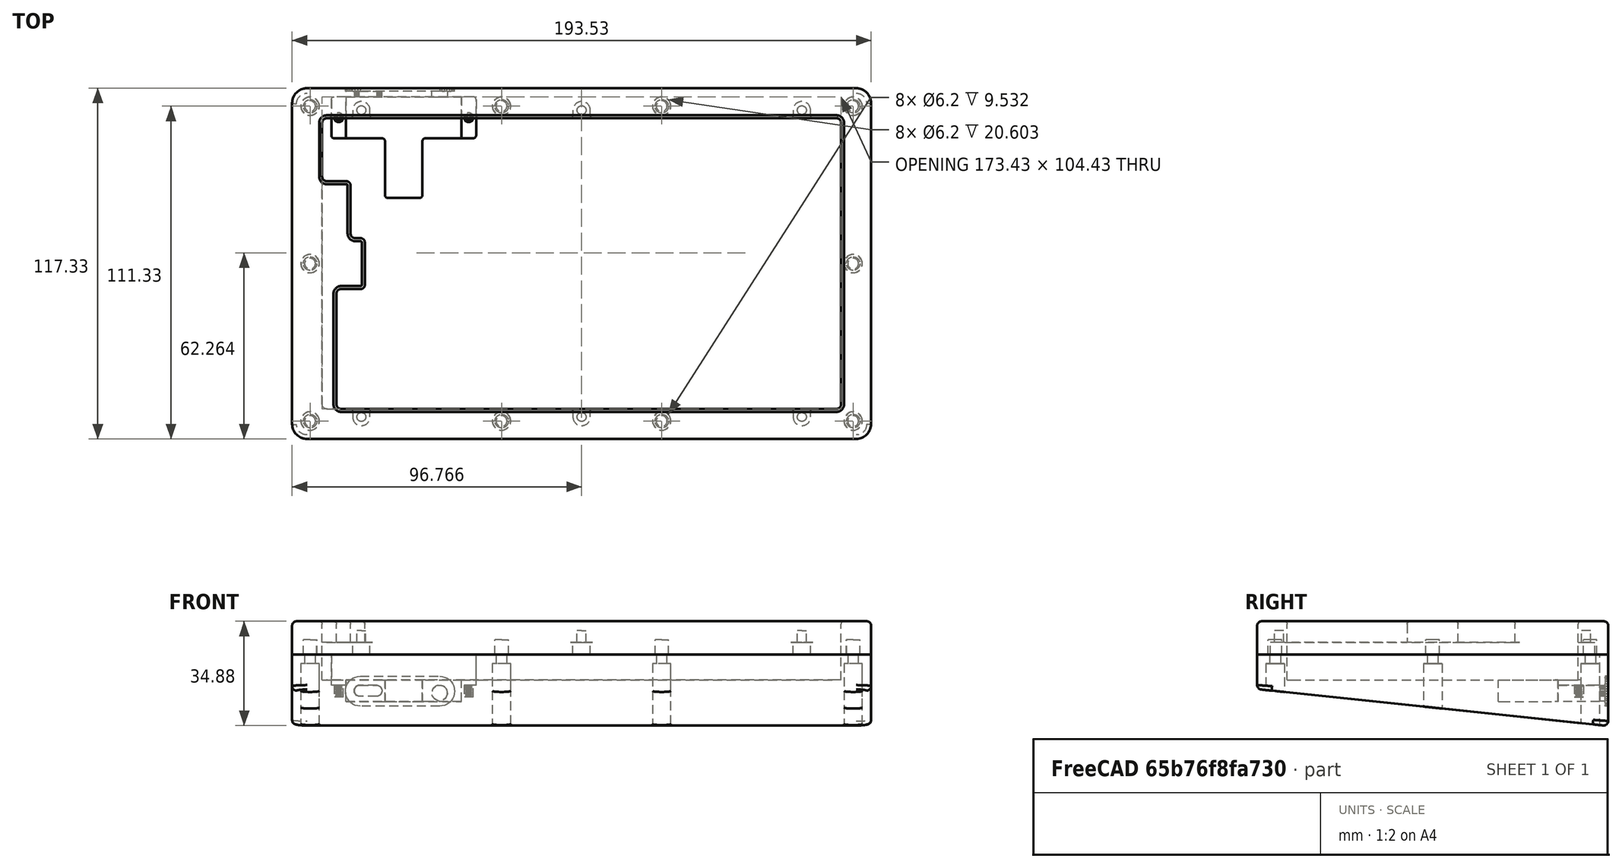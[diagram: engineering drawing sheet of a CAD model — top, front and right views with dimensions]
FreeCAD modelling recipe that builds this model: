
FCSTD DOCUMENT  (FreeCAD 0.21R33771 (Git))
Label: case_right
License: All rights reserved
LicenseURL: https://en.wikipedia.org/wiki/All_rights_reserved
objects: Part::Cylinder×44, Part::MultiFuse×39, Part::Feature×30, Part::Cut×18, Part::Fillet×18, Part::Extrusion×10, Part::Box×7, Part::FeaturePython×2
note: 168 computed .brp shape members not serialized (recipe doc carries the construction recipe); baked Part::Feature solids carry a one-line shape summary decoded from their .brp

FEATURE [Part::Box] Box  label="立方体"
  AttacherType = Attacher::AttachEngine3D
  Height = 11.2
  Length = 193.53
  Placement = pos=(0,-117.33,0) rot=(0,0,1;0rad)
  Width = 117.33
FEATURE [Part::Feature] rect39 .. rect048  x10 (patterned run collapsed; names and placements below)
  shape: bbox 4.5 x 4.5 x 2e-07 mm, 0 faces, 0 solids (baked)
FEATURE [Part::Feature] rect049
  shape: bbox 173.4 x 108.4 x 2e-07 mm, 0 faces, 0 solids (baked)
FEATURE [Part::MultiFuse] Fusion
  Shapes = -> [rect048,rect39,rect040,rect041,rect042,rect043,rect044,rect045,rect046,rect047]
FEATURE [Part::Extrusion] Extrude
  Base = -> Fusion
  Dir = (0,0,1)
  DirMode = 0
  FaceMakerClass = Part::FaceMakerBullseye
  LengthFwd = 5
  LengthRev = 0
  Solid = true
  Symmetric = false
FEATURE [Part::Cut] Cut
  Base = -> Box
  Tool = -> Extrude
FEATURE [Part::Extrusion] Extrude001
  Base = -> rect049
  Dir = (0,0,1)
  DirMode = 2
  FaceMakerClass = Part::FaceMakerBullseye
  LengthFwd = 4.1
  LengthRev = 0
  Solid = true
  Symmetric = false
FEATURE [Part::Cut] Cut001
  Base = -> Cut
  Tool = -> Extrude001
FEATURE [Part::Fillet] Fillet
  Base = -> Cut001
  Edges = 4 edges r=1.5: [Edge146,Edge148,Edge180,Edge182]
FEATURE [Part::Fillet] Fillet001
  Base = -> Fillet
  Edges = 12 edges r=0.8: [Edge83,Edge99,Edge100,Edge104,Edge115,Edge119,Edge120,Edge124,Edge135,Edge139,Edge140,Edge155]
FEATURE [Part::Fillet] Fillet002
  Base = -> Fillet001
  Edges = 4 edges r=5: [Edge195,Edge197,Edge198,Edge201]
FEATURE [Part::Feature] path6845_6_2_7_8_1 .. path6845_6_2_7_8_006  x6 (patterned run collapsed; names and placements below)
  shape: bbox 3 x 3 x 2e-07 mm, 0 faces, 0 solids (baked)
FEATURE [Part::MultiFuse] Fusion001
  Shapes = -> [path6845_6_2_7_8_006,path6845_6_2_7_8_1,path6845_6_2_7_8_002,path6845_6_2_7_8_003,path6845_6_2_7_8_004,path6845_6_2_7_8_005]
FEATURE [Part::Extrusion] Extrude002
  Base = -> Fusion001
  Dir = (0,0,1)
  DirMode = 0
  FaceMakerClass = Part::FaceMakerBullseye
  LengthFwd = 4
  LengthRev = 0
  Placement = pos=(0,0,4.1) rot=(0,0,1;0rad)
  Solid = true
  Symmetric = false
FEATURE [Part::Cut] Cut002
  Base = -> Fillet002
  Tool = -> Extrude002
FEATURE [Part::Feature] path48_5
  shape: bbox 173.4 x 97.23 x 2e-07 mm, 0 faces, 0 solids (baked)
FEATURE [Part::Extrusion] Extrude003
  Base = -> path48_5
  Dir = (0,0,1)
  DirMode = 0
  FaceMakerClass = Part::FaceMakerBullseye
  LengthFwd = 7.1
  LengthRev = 0
  Placement = pos=(0,0,4.1) rot=(0,0,1;0rad)
  Solid = true
  Symmetric = false
FEATURE [Part::Fillet] Fillet003
  Base = -> Extrude003
  Edges = 10 edges r=1.5: [Edge1,Edge2,Edge5,Edge8,Edge11,Edge14,Edge17,Edge20,Edge23,Edge26]
FEATURE [Part::Cut] Cut003
  Base = -> Cut002
  Tool = -> Fillet003
FEATURE [Part::Fillet] Fillet004
  Base = -> Cut003
  Edges = 8 edges r=1.5: [Edge99,Edge103,Edge104,Edge107,Edge108,Edge111,Edge113,Edge114]
FEATURE [Part::Fillet] Fillet005  label="top_right"
  Base = -> Fillet004
  Edges = 20 edges r=1: [Edge119,Edge120,Edge121,Edge122,Edge123,Edge124,Edge125,Edge126,Edge127,Edge128,Edge129,Edge130,Edge131,Edge132,Edge133,Edge134,Edge135,Edge136,Edge137,Edge138]
  Placement = pos=(0,0,10) rot=(0,0,1;0rad)
FEATURE [Part::Box] Box001  label="立方体001"
  AttacherType = Attacher::AttachEngine3D
  Height = 30
  Length = 193.53
  Placement = pos=(0,-117.33,-20) rot=(0,0,1;0rad)
  Width = 117.33
FEATURE [Part::Box] Box002  label="立方体002"
  AttacherType = Attacher::AttachEngine3D
  Height = 100
  Length = 193.53
  Placement = pos=(0,-129.33,-100.8) rot=(-1,0,0;0.10472rad)
  Width = 150
FEATURE [Part::Cut] Cut004
  Base = -> Box001
  Tool = -> Box002
FEATURE [Part::Cylinder] Cylinder045  label="円柱045"
  Angle = 360
  AttacherType = Attacher::AttachEngine3D
  FirstAngle = 0
  Height = 30
  Placement = pos=(0,0,-32) rot=(0,0,1;0rad)
  Radius = 3.1
  SecondAngle = 0
FEATURE [Part::Cylinder] Cylinder046  label="円柱046"
  Angle = 360
  AttacherType = Attacher::AttachEngine3D
  FirstAngle = 0
  Height = 20
  Placement = pos=(0,0,-10) rot=(0,0,1;0rad)
  Radius = 1.8
  SecondAngle = 0
FEATURE [Part::Cylinder] Cylinder047  label="円柱047"
  Angle = 360
  AttacherType = Attacher::AttachEngine3D
  FirstAngle = 0
  Height = 30
  Placement = pos=(0,0,-32) rot=(0,0,1;0rad)
  Radius = 3.1
  SecondAngle = 0
FEATURE [Part::Cylinder] Cylinder048  label="円柱048"
  Angle = 360
  AttacherType = Attacher::AttachEngine3D
  FirstAngle = 0
  Height = 20
  Placement = pos=(0,0,-10) rot=(0,0,1;0rad)
  Radius = 1.8
  SecondAngle = 0
FEATURE [Part::Cylinder] Cylinder049  label="円柱049"
  Angle = 360
  AttacherType = Attacher::AttachEngine3D
  FirstAngle = 0
  Height = 30
  Placement = pos=(0,0,-32) rot=(0,0,1;0rad)
  Radius = 3.1
  SecondAngle = 0
FEATURE [Part::Cylinder] Cylinder050  label="円柱050"
  Angle = 360
  AttacherType = Attacher::AttachEngine3D
  FirstAngle = 0
  Height = 20
  Placement = pos=(0,0,-10) rot=(0,0,1;0rad)
  Radius = 1.8
  SecondAngle = 0
FEATURE [Part::Cylinder] Cylinder051  label="円柱051"
  Angle = 360
  AttacherType = Attacher::AttachEngine3D
  FirstAngle = 0
  Height = 30
  Placement = pos=(0,0,-32) rot=(0,0,1;0rad)
  Radius = 3.1
  SecondAngle = 0
FEATURE [Part::Cylinder] Cylinder052  label="円柱052"
  Angle = 360
  AttacherType = Attacher::AttachEngine3D
  FirstAngle = 0
  Height = 20
  Placement = pos=(0,0,-10) rot=(0,0,1;0rad)
  Radius = 1.8
  SecondAngle = 0
FEATURE [Part::Cylinder] Cylinder055  label="円柱055"
  Angle = 360
  AttacherType = Attacher::AttachEngine3D
  FirstAngle = 0
  Height = 30
  Placement = pos=(0,0,-32) rot=(0,0,1;0rad)
  Radius = 3.1
  SecondAngle = 0
FEATURE [Part::Cylinder] Cylinder056  label="円柱056"
  Angle = 360
  AttacherType = Attacher::AttachEngine3D
  FirstAngle = 0
  Height = 20
  Placement = pos=(0,0,-10) rot=(0,0,1;0rad)
  Radius = 1.8
  SecondAngle = 0
FEATURE [Part::Cylinder] Cylinder057  label="円柱057"
  Angle = 360
  AttacherType = Attacher::AttachEngine3D
  FirstAngle = 0
  Height = 30
  Placement = pos=(0,0,-32) rot=(0,0,1;0rad)
  Radius = 3.1
  SecondAngle = 0
FEATURE [Part::Cylinder] Cylinder058  label="円柱058"
  Angle = 360
  AttacherType = Attacher::AttachEngine3D
  FirstAngle = 0
  Height = 20
  Placement = pos=(0,0,-10) rot=(0,0,1;0rad)
  Radius = 1.8
  SecondAngle = 0
FEATURE [Part::Cylinder] Cylinder061  label="円柱061"
  Angle = 360
  AttacherType = Attacher::AttachEngine3D
  FirstAngle = 0
  Height = 30
  Placement = pos=(0,0,-32) rot=(0,0,1;0rad)
  Radius = 3.1
  SecondAngle = 0
FEATURE [Part::Cylinder] Cylinder062  label="円柱062"
  Angle = 360
  AttacherType = Attacher::AttachEngine3D
  FirstAngle = 0
  Height = 20
  Placement = pos=(0,0,-10) rot=(0,0,1;0rad)
  Radius = 1.8
  SecondAngle = 0
FEATURE [Part::Cylinder] Cylinder063  label="円柱063"
  Angle = 360
  AttacherType = Attacher::AttachEngine3D
  FirstAngle = 0
  Height = 30
  Placement = pos=(0,0,-32) rot=(0,0,1;0rad)
  Radius = 3.1
  SecondAngle = 0
FEATURE [Part::Cylinder] Cylinder064  label="円柱064"
  Angle = 360
  AttacherType = Attacher::AttachEngine3D
  FirstAngle = 0
  Height = 20
  Placement = pos=(0,0,-10) rot=(0,0,1;0rad)
  Radius = 1.8
  SecondAngle = 0
FEATURE [Part::Cylinder] Cylinder065  label="円柱065"
  Angle = 360
  AttacherType = Attacher::AttachEngine3D
  FirstAngle = 0
  Height = 30
  Placement = pos=(0,0,-32) rot=(0,0,1;0rad)
  Radius = 3.1
  SecondAngle = 0
FEATURE [Part::Cylinder] Cylinder066  label="円柱066"
  Angle = 360
  AttacherType = Attacher::AttachEngine3D
  FirstAngle = 0
  Height = 20
  Placement = pos=(0,0,-10) rot=(0,0,1;0rad)
  Radius = 1.8
  SecondAngle = 0
FEATURE [Part::Cylinder] Cylinder067  label="円柱067"
  Angle = 360
  AttacherType = Attacher::AttachEngine3D
  FirstAngle = 0
  Height = 30
  Placement = pos=(0,0,-32) rot=(0,0,1;0rad)
  Radius = 3.1
  SecondAngle = 0
FEATURE [Part::Cylinder] Cylinder068  label="円柱068"
  Angle = 360
  AttacherType = Attacher::AttachEngine3D
  FirstAngle = 0
  Height = 20
  Placement = pos=(0,0,-10) rot=(0,0,1;0rad)
  Radius = 1.8
  SecondAngle = 0
FEATURE [Part::Fillet] Fillet006
  Base = -> Cut004
  Edges = 4 edges r=5: [Edge1,Edge3,Edge5,Edge10]
FEATURE [Part::Fillet] Fillet007
  Base = -> Fillet006
  Edges = 8 edges r=1.5: [Edge3,Edge12,Edge14,Edge16,Edge17,Edge18,Edge19,Edge20]
FEATURE [Part::MultiFuse] Fusion048
  Placement = pos=(6,-6,0) rot=(0,0,1;0rad)
  Shapes = -> [Cylinder046,Cylinder045]
FEATURE [Part::MultiFuse] Fusion049
  Placement = pos=(6,-58.67,0) rot=(0,0,1;0rad)
  Shapes = -> [Cylinder048,Cylinder047]
FEATURE [Part::MultiFuse] Fusion050
  Placement = pos=(6,-111.34,0) rot=(0,0,1;0rad)
  Shapes = -> [Cylinder050,Cylinder049]
FEATURE [Part::MultiFuse] Fusion051
  Shapes = -> [Fusion050,Fusion049,Fusion048]
FEATURE [Part::MultiFuse] Fusion052
  Placement = pos=(6,-6,0) rot=(0,0,1;0rad)
  Shapes = -> [Cylinder052,Cylinder051]
FEATURE [Part::MultiFuse] Fusion054
  Placement = pos=(6,-111.34,0) rot=(0,0,1;0rad)
  Shapes = -> [Cylinder056,Cylinder055]
FEATURE [Part::MultiFuse] Fusion055
  Placement = pos=(64,0,0) rot=(0,0,1;0rad)
  Shapes = -> [Fusion054,Fusion052]
FEATURE [Part::MultiFuse] Fusion056
  Placement = pos=(6,-6,0) rot=(0,0,1;0rad)
  Shapes = -> [Cylinder058,Cylinder057]
FEATURE [Part::MultiFuse] Fusion058
  Placement = pos=(6,-111.34,0) rot=(0,0,1;0rad)
  Shapes = -> [Cylinder062,Cylinder061]
FEATURE [Part::MultiFuse] Fusion059
  Placement = pos=(117.53,0,0) rot=(0,0,1;0rad)
  Shapes = -> [Fusion058,Fusion056]
FEATURE [Part::MultiFuse] Fusion060
  Placement = pos=(6,-6,0) rot=(0,0,1;0rad)
  Shapes = -> [Cylinder064,Cylinder063]
FEATURE [Part::MultiFuse] Fusion061
  Placement = pos=(6,-58.67,0) rot=(0,0,1;0rad)
  Shapes = -> [Cylinder066,Cylinder065]
FEATURE [Part::MultiFuse] Fusion062
  Placement = pos=(6,-111.34,0) rot=(0,0,1;0rad)
  Shapes = -> [Cylinder068,Cylinder067]
FEATURE [Part::MultiFuse] Fusion063
  Placement = pos=(181.53,0,0) rot=(0,0,1;0rad)
  Shapes = -> [Fusion062,Fusion061,Fusion060]
FEATURE [Part::MultiFuse] Fusion064
  Placement = pos=(0,0,9) rot=(0,0,1;0rad)
  Shapes = -> [Fusion063,Fusion059,Fusion055,Fusion051]
FEATURE [Part::Cut] Cut005
  Base = -> Fillet007
  Tool = -> Fusion064
FEATURE [Part::Feature] path6845_6_2_7_83_9
  shape: bbox 173.4 x 97.23 x 2e-07 mm, 0 faces, 0 solids (baked)
FEATURE [Part::Extrusion] Extrude004
  Base = -> path6845_6_2_7_83_9
  Dir = (0,0,1)
  DirMode = 0
  FaceMakerClass = Part::FaceMakerBullseye
  LengthFwd = 8.5
  LengthRev = 0
  Placement = pos=(0,0,1.5) rot=(0,0,1;0rad)
  Solid = true
  Symmetric = false
FEATURE [Part::Fillet] Fillet009
  Base = -> Extrude004
  Edges = 4 edges r=1.5: [Edge1,Edge2,Edge5,Edge8]
FEATURE [Part::Cut] Cut006
  Base = -> Cut005
  Tool = -> Fillet009
FEATURE [Part::Feature] rect3_6_21_5
  Placement = pos=(0,0,-0.2) rot=(0,0,1;0rad)
  shape: bbox 38.6 x 13.9 x 2e-07 mm, 0 faces, 0 solids (baked)
FEATURE [Part::Cylinder] Cylinder  label="円柱"
  Angle = 360
  AttacherType = Attacher::AttachEngine3D
  FirstAngle = 0
  Height = 4
  Placement = pos=(15.57,-9.8,-4.2) rot=(0,0,1;0rad)
  Radius = 1.55
  SecondAngle = 0
FEATURE [Part::Cylinder] Cylinder069  label="円柱069"
  Angle = 360
  AttacherType = Attacher::AttachEngine3D
  FirstAngle = 0
  Height = 4
  Placement = pos=(59.03,-9.8,-4.2) rot=(0,0,1;0rad)
  Radius = 1.55
  SecondAngle = 0
FEATURE [Part::MultiFuse] Fusion065
  Shapes = -> [Cylinder,Cylinder069]
FEATURE [Part::Feature] rect3_6_2
  Placement = pos=(0,0,-0.2) rot=(0,0,1;0rad)
  shape: bbox 48.4 x 13.9 x 2e-07 mm, 0 faces, 0 solids (baked)
FEATURE [Part::Extrusion] Extrude006
  Base = -> rect3_6_2
  Dir = (0,0,1)
  DirMode = 0
  FaceMakerClass = Part::FaceMakerBullseye
  LengthFwd = 16.7
  LengthRev = 0
  Solid = true
  Symmetric = false
FEATURE [Part::Fillet] Fillet010
  Base = -> Extrude006
  Edges = 4 edges r=1: [Edge1,Edge2,Edge5,Edge8]
FEATURE [Part::Extrusion] Extrude007
  Base = -> rect3_6_21_5
  Dir = (0,0,1)
  DirMode = 0
  FaceMakerClass = Part::FaceMakerBullseye
  LengthFwd = 22.2
  LengthRev = 0
  Placement = pos=(0,0,-5.5) rot=(0,0,1;0rad)
  Solid = true
  Symmetric = false
FEATURE [Part::Cylinder] Cylinder070  label="trrs"
  Angle = 360
  AttacherType = Attacher::AttachEngine3D
  FirstAngle = 0
  Height = 10
  Placement = pos=(49.3,5,-2.8) rot=(1,0,0;1.5708rad)
  Radius = 2.6
  SecondAngle = 0
FEATURE [Part::Box] Box003  label="立方体003"
  AttacherType = Attacher::AttachEngine3D
  Height = 7.2
  Length = 12.5
  Placement = pos=(31.05,-36.75,-5.7) rot=(0,0,1;0rad)
  Width = 20
FEATURE [Part::MultiFuse] Fusion066
  Shapes = -> [Extrude007,Box003]
FEATURE [Part::Feature] hull006
  Placement = pos=(0,4.8,0) rot=(0,0,1;0rad)
  shape: bbox 13.02 x 10 x 7.518 mm, 128 faces (baked)
FEATURE [Part::Feature] hull007
  shape: bbox 9.26 x 10 x 3.733 mm, 28 faces (baked)
FEATURE [Part::MultiFuse] Fusion067  label="usb-hole001"
  Placement = pos=(-290.45,-1.85,-4.55) rot=(0,0,1;0rad)
  Shapes = -> [hull006,hull007]
FEATURE [Part::MultiFuse] Fusion068
  Shapes = -> [Cylinder070,Fusion067,Fusion065]
FEATURE [Part::Cut] Cut007
  Base = -> Cut006
  Tool = -> Fusion066
FEATURE [Part::Fillet] Fillet011
  Base = -> Cut007
  Edges = 4 edges r=1: [Edge151,Edge152,Edge154,Edge156]
FEATURE [Part::Cut] Cut008
  Base = -> Fillet011
  Tool = -> Fillet010
FEATURE [Part::Feature] hull
  shape: bbox 36.5 x 3 x 10 mm, 40 faces (baked)
FEATURE [Part::Fillet] Fillet012
  Base = -> Cut008
  Edges = 2 edges r=1: [Edge53,Edge72]
FEATURE [Part::Cut] Cut009
  Base = -> Fillet012
  Tool = -> Fusion068
FEATURE [Part::Cut] Cut010  label="bottom_right"
  Base = -> Cut009
  Tool = -> hull
FEATURE [Part::Box] Box004  label="立方体004"
  AttacherType = Attacher::AttachEngine3D
  Height = 30
  Length = 193.53
  Placement = pos=(0,-117.33,-20) rot=(0,0,1;0rad)
  Width = 117.33
FEATURE [Part::Box] Box005  label="立方体005"
  AttacherType = Attacher::AttachEngine3D
  Height = 100
  Length = 193.53
  Placement = pos=(0,-129.33,-100.8) rot=(-1,0,0;0.10472rad)
  Width = 150
FEATURE [Part::Box] Box006  label="立方体006"
  AttacherType = Attacher::AttachEngine3D
  Height = 7.2
  Length = 12.5
  Placement = pos=(31.05,-36.75,-5.7) rot=(0,0,1;0rad)
  Width = 20
FEATURE [Part::Cut] Cut011
  Base = -> Box004
  Tool = -> Box005
FEATURE [Part::Cylinder] Cylinder072  label="円柱071"
  Angle = 360
  AttacherType = Attacher::AttachEngine3D
  FirstAngle = 0
  Height = 30
  Placement = pos=(0,0,-32) rot=(0,0,1;0rad)
  Radius = 3.1
  SecondAngle = 0
FEATURE [Part::Cylinder] Cylinder073  label="円柱072"
  Angle = 360
  AttacherType = Attacher::AttachEngine3D
  FirstAngle = 0
  Height = 20
  Placement = pos=(0,0,-10) rot=(0,0,1;0rad)
  Radius = 1.8
  SecondAngle = 0
FEATURE [Part::Cylinder] Cylinder074  label="円柱073"
  Angle = 360
  AttacherType = Attacher::AttachEngine3D
  FirstAngle = 0
  Height = 30
  Placement = pos=(0,0,-32) rot=(0,0,1;0rad)
  Radius = 3.1
  SecondAngle = 0
FEATURE [Part::Cylinder] Cylinder075  label="円柱074"
  Angle = 360
  AttacherType = Attacher::AttachEngine3D
  FirstAngle = 0
  Height = 20
  Placement = pos=(0,0,-10) rot=(0,0,1;0rad)
  Radius = 1.8
  SecondAngle = 0
FEATURE [Part::Cylinder] Cylinder076  label="円柱075"
  Angle = 360
  AttacherType = Attacher::AttachEngine3D
  FirstAngle = 0
  Height = 30
  Placement = pos=(0,0,-32) rot=(0,0,1;0rad)
  Radius = 3.1
  SecondAngle = 0
FEATURE [Part::Cylinder] Cylinder077  label="円柱076"
  Angle = 360
  AttacherType = Attacher::AttachEngine3D
  FirstAngle = 0
  Height = 20
  Placement = pos=(0,0,-10) rot=(0,0,1;0rad)
  Radius = 1.8
  SecondAngle = 0
FEATURE [Part::Cylinder] Cylinder078  label="円柱077"
  Angle = 360
  AttacherType = Attacher::AttachEngine3D
  FirstAngle = 0
  Height = 30
  Placement = pos=(0,0,-32) rot=(0,0,1;0rad)
  Radius = 3.1
  SecondAngle = 0
FEATURE [Part::Cylinder] Cylinder079  label="円柱078"
  Angle = 360
  AttacherType = Attacher::AttachEngine3D
  FirstAngle = 0
  Height = 20
  Placement = pos=(0,0,-10) rot=(0,0,1;0rad)
  Radius = 1.8
  SecondAngle = 0
FEATURE [Part::Cylinder] Cylinder080  label="円柱079"
  Angle = 360
  AttacherType = Attacher::AttachEngine3D
  FirstAngle = 0
  Height = 30
  Placement = pos=(0,0,-32) rot=(0,0,1;0rad)
  Radius = 3.1
  SecondAngle = 0
FEATURE [Part::Cylinder] Cylinder081  label="円柱080"
  Angle = 360
  AttacherType = Attacher::AttachEngine3D
  FirstAngle = 0
  Height = 20
  Placement = pos=(0,0,-10) rot=(0,0,1;0rad)
  Radius = 1.8
  SecondAngle = 0
FEATURE [Part::Cylinder] Cylinder082  label="円柱081"
  Angle = 360
  AttacherType = Attacher::AttachEngine3D
  FirstAngle = 0
  Height = 30
  Placement = pos=(0,0,-32) rot=(0,0,1;0rad)
  Radius = 3.1
  SecondAngle = 0
FEATURE [Part::Cylinder] Cylinder083  label="円柱082"
  Angle = 360
  AttacherType = Attacher::AttachEngine3D
  FirstAngle = 0
  Height = 20
  Placement = pos=(0,0,-10) rot=(0,0,1;0rad)
  Radius = 1.8
  SecondAngle = 0
FEATURE [Part::Cylinder] Cylinder084  label="円柱083"
  Angle = 360
  AttacherType = Attacher::AttachEngine3D
  FirstAngle = 0
  Height = 30
  Placement = pos=(0,0,-32) rot=(0,0,1;0rad)
  Radius = 3.1
  SecondAngle = 0
FEATURE [Part::Cylinder] Cylinder085  label="円柱084"
  Angle = 360
  AttacherType = Attacher::AttachEngine3D
  FirstAngle = 0
  Height = 20
  Placement = pos=(0,0,-10) rot=(0,0,1;0rad)
  Radius = 1.8
  SecondAngle = 0
FEATURE [Part::Cylinder] Cylinder086  label="円柱085"
  Angle = 360
  AttacherType = Attacher::AttachEngine3D
  FirstAngle = 0
  Height = 30
  Placement = pos=(0,0,-32) rot=(0,0,1;0rad)
  Radius = 3.1
  SecondAngle = 0
FEATURE [Part::Cylinder] Cylinder087  label="円柱086"
  Angle = 360
  AttacherType = Attacher::AttachEngine3D
  FirstAngle = 0
  Height = 20
  Placement = pos=(0,0,-10) rot=(0,0,1;0rad)
  Radius = 1.8
  SecondAngle = 0
FEATURE [Part::Cylinder] Cylinder088  label="円柱087"
  Angle = 360
  AttacherType = Attacher::AttachEngine3D
  FirstAngle = 0
  Height = 30
  Placement = pos=(0,0,-32) rot=(0,0,1;0rad)
  Radius = 3.1
  SecondAngle = 0
FEATURE [Part::Cylinder] Cylinder089  label="円柱088"
  Angle = 360
  AttacherType = Attacher::AttachEngine3D
  FirstAngle = 0
  Height = 20
  Placement = pos=(0,0,-10) rot=(0,0,1;0rad)
  Radius = 1.8
  SecondAngle = 0
FEATURE [Part::Cylinder] Cylinder090  label="円柱089"
  Angle = 360
  AttacherType = Attacher::AttachEngine3D
  FirstAngle = 0
  Height = 30
  Placement = pos=(0,0,-32) rot=(0,0,1;0rad)
  Radius = 3.1
  SecondAngle = 0
FEATURE [Part::Cylinder] Cylinder091  label="円柱090"
  Angle = 360
  AttacherType = Attacher::AttachEngine3D
  FirstAngle = 0
  Height = 20
  Placement = pos=(0,0,-10) rot=(0,0,1;0rad)
  Radius = 1.8
  SecondAngle = 0
FEATURE [Part::Cylinder] Cylinder093  label="trrs001"
  Angle = 360
  AttacherType = Attacher::AttachEngine3D
  FirstAngle = 0
  Height = 10
  Placement = pos=(49.3,5,-2.8) rot=(1,0,0;1.5708rad)
  Radius = 2.6
  SecondAngle = 0
FEATURE [Part::Fillet] Fillet013
  Base = -> Cut011
  Edges = 4 edges r=5: [Edge1,Edge3,Edge5,Edge10]
FEATURE [Part::Fillet] Fillet014
  Base = -> Fillet013
  Edges = 8 edges r=1.5: [Edge3,Edge12,Edge14,Edge16,Edge17,Edge18,Edge19,Edge20]
FEATURE [Part::MultiFuse] Fusion069
  Placement = pos=(6,-6,0) rot=(0,0,1;0rad)
  Shapes = -> [Cylinder073,Cylinder072]
FEATURE [Part::MultiFuse] Fusion070
  Placement = pos=(6,-58.67,0) rot=(0,0,1;0rad)
  Shapes = -> [Cylinder075,Cylinder074]
FEATURE [Part::MultiFuse] Fusion071
  Placement = pos=(6,-111.34,0) rot=(0,0,1;0rad)
  Shapes = -> [Cylinder077,Cylinder076]
FEATURE [Part::MultiFuse] Fusion072
  Shapes = -> [Fusion071,Fusion070,Fusion069]
FEATURE [Part::MultiFuse] Fusion073
  Placement = pos=(6,-6,0) rot=(0,0,1;0rad)
  Shapes = -> [Cylinder079,Cylinder078]
FEATURE [Part::MultiFuse] Fusion074
  Placement = pos=(6,-111.34,0) rot=(0,0,1;0rad)
  Shapes = -> [Cylinder081,Cylinder080]
FEATURE [Part::MultiFuse] Fusion075
  Placement = pos=(64,0,0) rot=(0,0,1;0rad)
  Shapes = -> [Fusion074,Fusion073]
FEATURE [Part::MultiFuse] Fusion076
  Placement = pos=(6,-6,0) rot=(0,0,1;0rad)
  Shapes = -> [Cylinder083,Cylinder082]
FEATURE [Part::MultiFuse] Fusion077
  Placement = pos=(6,-111.34,0) rot=(0,0,1;0rad)
  Shapes = -> [Cylinder085,Cylinder084]
FEATURE [Part::MultiFuse] Fusion078
  Placement = pos=(117.53,0,0) rot=(0,0,1;0rad)
  Shapes = -> [Fusion077,Fusion076]
FEATURE [Part::MultiFuse] Fusion079
  Placement = pos=(6,-6,0) rot=(0,0,1;0rad)
  Shapes = -> [Cylinder087,Cylinder086]
FEATURE [Part::MultiFuse] Fusion080
  Placement = pos=(6,-58.67,0) rot=(0,0,1;0rad)
  Shapes = -> [Cylinder089,Cylinder088]
FEATURE [Part::MultiFuse] Fusion081
  Placement = pos=(6,-111.34,0) rot=(0,0,1;0rad)
  Shapes = -> [Cylinder091,Cylinder090]
FEATURE [Part::MultiFuse] Fusion082
  Placement = pos=(181.53,0,0) rot=(0,0,1;0rad)
  Shapes = -> [Fusion081,Fusion080,Fusion079]
FEATURE [Part::MultiFuse] Fusion083
  Placement = pos=(0,0,9) rot=(0,0,1;0rad)
  Shapes = -> [Fusion082,Fusion078,Fusion075,Fusion072]
FEATURE [Part::Cut] Cut012
  Base = -> Fillet014
  Tool = -> Fusion083
FEATURE [Part::Feature] hull008
  shape: bbox 36.5 x 3 x 10 mm, 40 faces (baked)
FEATURE [Part::Feature] hull009
  Placement = pos=(0,4.8,0) rot=(0,0,1;0rad)
  shape: bbox 13.02 x 10 x 7.518 mm, 128 faces (baked)
FEATURE [Part::Feature] hull010
  shape: bbox 9.26 x 10 x 3.733 mm, 28 faces (baked)
FEATURE [Part::MultiFuse] Fusion086  label="usb-hole002"
  Placement = pos=(-290.45,-1.85,-4.55) rot=(0,0,1;0rad)
  Shapes = -> [hull009,hull010]
FEATURE [Part::Feature] path6845_6_2_7_83_010
  shape: bbox 173.4 x 97.23 x 2e-07 mm, 0 faces, 0 solids (baked)
FEATURE [Part::Extrusion] Extrude008
  Base = -> path6845_6_2_7_83_010
  Dir = (0,0,1)
  DirMode = 0
  FaceMakerClass = Part::FaceMakerBullseye
  LengthFwd = 8.5
  LengthRev = 0
  Placement = pos=(0,0,1.5) rot=(0,0,1;0rad)
  Solid = true
  Symmetric = false
FEATURE [Part::Fillet] Fillet015
  Base = -> Extrude008
  Edges = 4 edges r=1.5: [Edge1,Edge2,Edge5,Edge8]
FEATURE [Part::Cut] Cut013
  Base = -> Cut012
  Tool = -> Fillet015
FEATURE [Part::Feature] rect3_6_003
  Placement = pos=(0,0,-0.2) rot=(0,0,1;0rad)
  shape: bbox 48.4 x 13.9 x 2e-07 mm, 0 faces, 0 solids (baked)
FEATURE [Part::Extrusion] Extrude009
  Base = -> rect3_6_003
  Dir = (0,0,1)
  DirMode = 0
  FaceMakerClass = Part::FaceMakerBullseye
  LengthFwd = 16.7
  LengthRev = 0
  Solid = true
  Symmetric = false
FEATURE [Part::Fillet] Fillet016
  Base = -> Extrude009
  Edges = 4 edges r=1: [Edge1,Edge2,Edge5,Edge8]
FEATURE [Part::Feature] rect3_6_21_006
  Placement = pos=(0,0,-0.2) rot=(0,0,1;0rad)
  shape: bbox 38.6 x 13.9 x 2e-07 mm, 0 faces, 0 solids (baked)
FEATURE [Part::Extrusion] Extrude010
  Base = -> rect3_6_21_006
  Dir = (0,0,1)
  DirMode = 0
  FaceMakerClass = Part::FaceMakerBullseye
  LengthFwd = 22.2
  LengthRev = 0
  Placement = pos=(0,0,-5.5) rot=(0,0,1;0rad)
  Solid = true
  Symmetric = false
FEATURE [Part::MultiFuse] Fusion085
  Shapes = -> [Extrude010,Box006]
FEATURE [Part::Cut] Cut014
  Base = -> Cut013
  Tool = -> Fusion085
FEATURE [Part::Fillet] Fillet017
  Base = -> Cut014
  Edges = 4 edges r=1: [Edge151,Edge152,Edge154,Edge156]
FEATURE [Part::Cut] Cut015
  Base = -> Fillet017
  Tool = -> Fillet016
FEATURE [Part::Fillet] Fillet018
  Base = -> Cut015
  Edges = 2 edges r=1: [Edge53,Edge72]
FEATURE [Part::FeaturePython] ThreadedRod  label="M2x5-ThreadedRod001"  # Fasteners workbench fastener (typed FeaturePython)
  Placement = pos=(15.57,-9.8,0.8) rot=(0,0,1;0rad)
  diameter = 2
  diameterCustom = 6
  invert = false
  leftHanded = false
  length = 5
  matchOuter = false
  offset = 0
  pitchCustom = 1
  thread = true
  type = 4
FEATURE [Part::FeaturePython] ThreadedRod001  label="M2x5-ThreadedRod"  # Fasteners workbench fastener (typed FeaturePython)
  Placement = pos=(59.03,-9.8,0.8) rot=(0,0,1;0rad)
  diameter = 2
  diameterCustom = 6
  invert = false
  leftHanded = false
  length = 5
  matchOuter = false
  offset = 0
  pitchCustom = 1
  thread = true
  type = 4
FEATURE [Part::MultiFuse] Fusion087
  Shapes = -> [ThreadedRod,ThreadedRod001,Fusion086,Cylinder093]
FEATURE [Part::Cut] Cut016
  Base = -> Fillet018
  Tool = -> Fusion087
FEATURE [Part::Cut] Cut017  label="bottom_right_resin"
  Base = -> Cut016
  Tool = -> hull008
